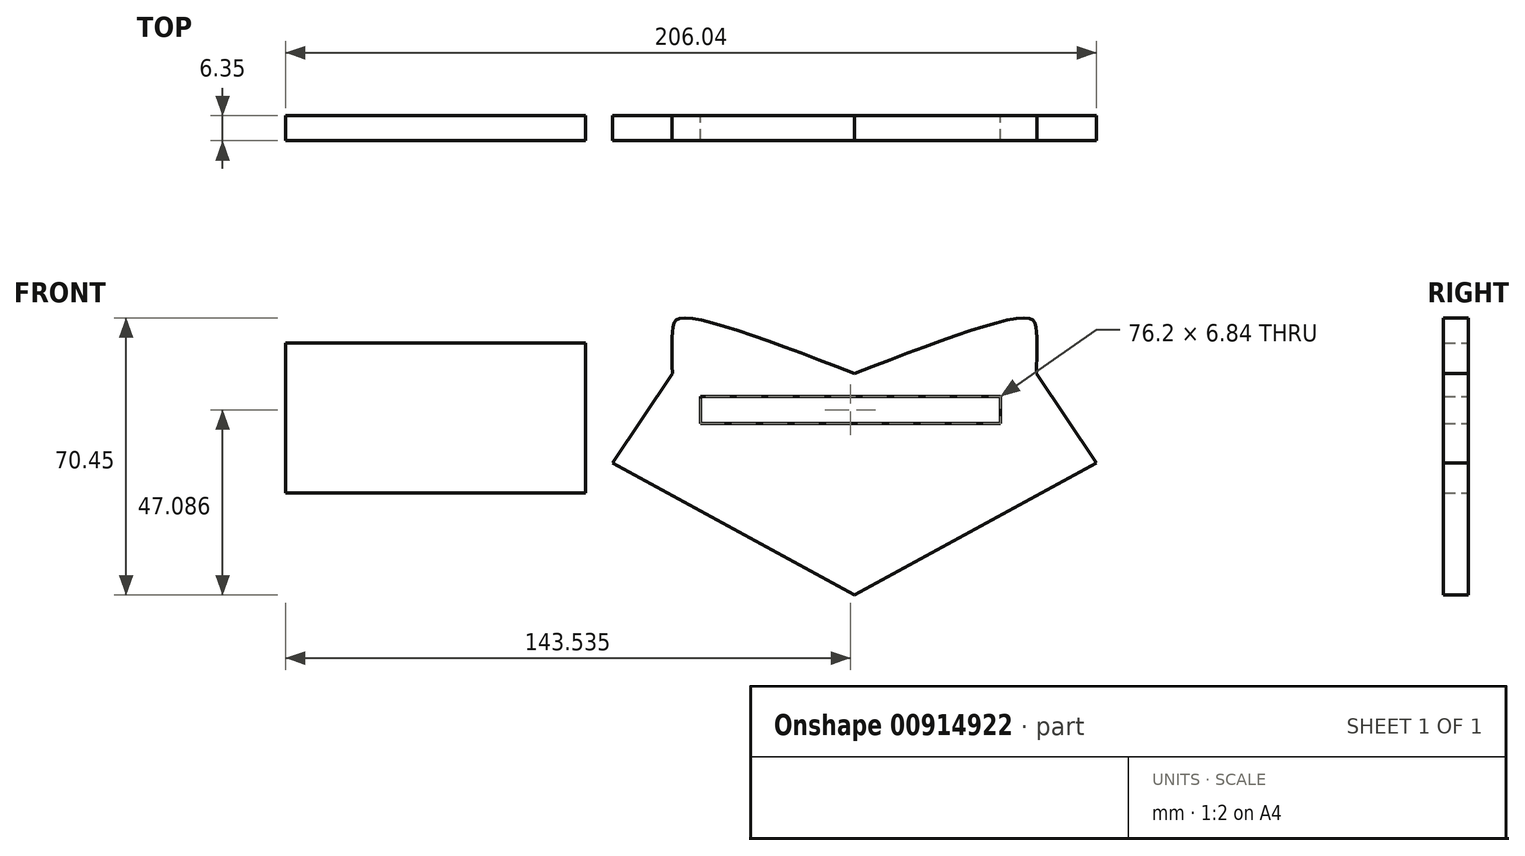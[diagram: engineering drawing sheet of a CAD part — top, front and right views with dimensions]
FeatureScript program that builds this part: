
annotation { "Feature Type Name" : "Feature", "Feature Type Description" : "" }
export const myFeature = defineFeature(function(context is Context, id is Id, definition is map)
    precondition{}
    {
        {
            var Q0;
            Q0=qCreatedBy(makeId("Front.planeOp"),FACE);
            var sketch = newSketch(context, id + "F0", { "sketchPlane" : qUnion([Q0])});
            skLineSegment(sketch, "E0", {"start": v(0, 48.44) * mm, "end": v(46.22, 48.44) * mm});
            skLineSegment(sketch, "E1", {"start": v(46.22, 48.44) * mm, "end": v(61.5, 25.74) * mm});
            skLineSegment(sketch, "E2", {"start": v(61.5, 25.74) * mm, "end": v(0, -7.87) * mm});
            skLineSegment(sketch, "E3.MirrorCS", {"start": v(-46.22, 48.44) * mm, "end": v(-61.5, 25.74) * mm});
            skLineSegment(sketch, "E4.MirrorCS", {"start": v(-61.5, 25.74) * mm, "end": v(0, -7.87) * mm});
            skLineSegment(sketch, "E5.MirrorCS", {"start": v(0, 48.44) * mm, "end": v(-46.22, 48.44) * mm});
            skFitSpline(sketch, "E6", {"points": [v(-46.22, 48.44) * mm, v(-46.22, 59.58) * mm, v(-44.58, 62.42) * mm, v(0, 48.44) * mm], "startDerivative": vector(-1.25, 45.48) * mm, "endDerivative": vector(104.5, -40.42) * mm});
            skFitSpline(sketch, "E7.MirrorCS", {"points": [v(46.22, 48.44) * mm, v(46.22, 59.58) * mm, v(44.58, 62.42) * mm, v(0, 48.44) * mm], "startDerivative": vector(1.25, 45.48) * mm, "endDerivative": vector(-104.5, -40.42) * mm});
            skLineSegment(sketch, "E8.bottom", {"start": v(-39.1, 42.63) * mm, "end": v(37.1, 42.63) * mm});
            skLineSegment(sketch, "E8.top", {"start": v(-39.1, 35.8) * mm, "end": v(37.1, 35.8) * mm});
            skLineSegment(sketch, "E8.left", {"start": v(-39.1, 42.63) * mm, "end": v(-39.1, 35.8) * mm});
            skLineSegment(sketch, "E8.right", {"start": v(37.1, 42.63) * mm, "end": v(37.1, 35.8) * mm});
            skLineSegment(sketch, "E9.bottom", {"start": v(-144.54, 56.14) * mm, "end": v(-68.34, 56.14) * mm});
            skLineSegment(sketch, "E9.top", {"start": v(-144.54, 18.04) * mm, "end": v(-68.34, 18.04) * mm});
            skLineSegment(sketch, "E9.left", {"start": v(-144.54, 56.14) * mm, "end": v(-144.54, 18.04) * mm});
            skLineSegment(sketch, "E9.right", {"start": v(-68.34, 56.14) * mm, "end": v(-68.34, 18.04) * mm});
            skSolve(sketch);
        }
        {
            var Q0;
            Q0 = qSketchRegion(id + "F0", true);
            extrude(context, id + "F1", {"entities" : qUnion([Q0]), "depth" : 6.35 * mm, "offsetDistance" : 25.4 * mm});
        }
    });
